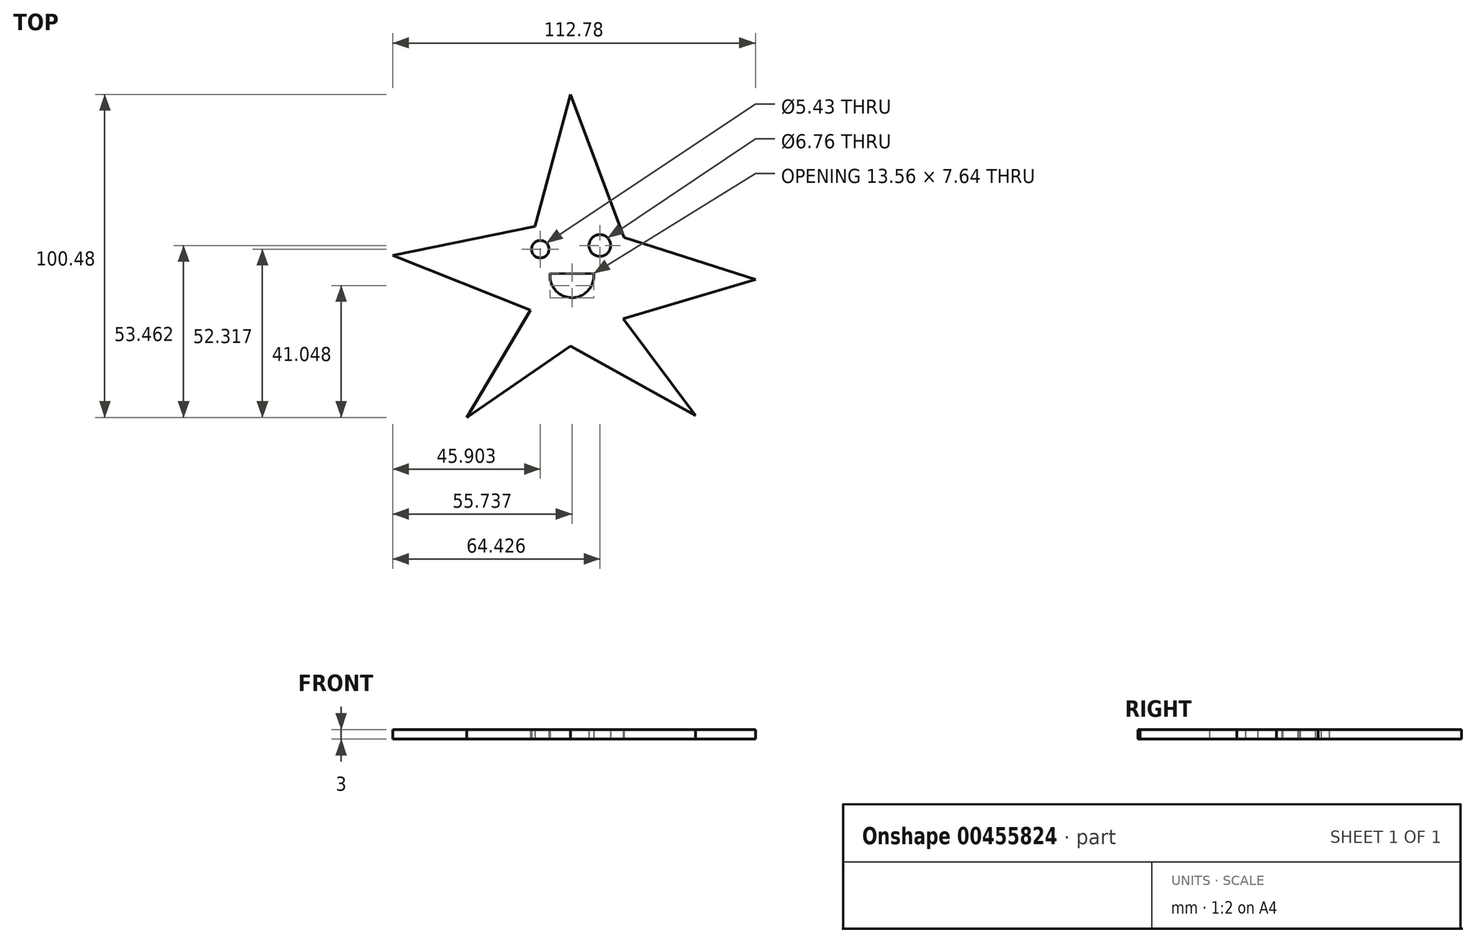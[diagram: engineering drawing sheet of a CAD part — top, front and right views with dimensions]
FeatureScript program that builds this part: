
annotation { "Feature Type Name" : "Feature", "Feature Type Description" : "" }
export const myFeature = defineFeature(function(context is Context, id is Id, definition is map)
    precondition{}
    {
        {
            var Q0;
            Q0=qCreatedBy(makeId("Top.planeOp"),FACE);
            var sketch = newSketch(context, id + "F0", { "sketchPlane" : qUnion([Q0])});
            skLineSegment(sketch, "E0", {"start": v(0, 57.52) * mm, "end": v(16.61, 12.98) * mm});
            skLineSegment(sketch, "E1", {"start": v(16.61, 12.98) * mm, "end": v(57.52, 0) * mm});
            skLineSegment(sketch, "E2", {"start": v(57.52, 0) * mm, "end": v(16.42, -12.22) * mm});
            skLineSegment(sketch, "E3", {"start": v(16.42, -12.22) * mm, "end": v(38.88, -42.38) * mm});
            skLineSegment(sketch, "E4", {"start": v(38.88, -42.38) * mm, "end": v(0, -20.81) * mm});
            skLineSegment(sketch, "E5", {"start": v(0, -20.81) * mm, "end": v(-32.27, -42.96) * mm});
            skLineSegment(sketch, "E6", {"start": v(-32.27, -42.96) * mm, "end": v(-12.41, -9.55) * mm});
            skLineSegment(sketch, "E7", {"start": v(-12.41, -9.55) * mm, "end": v(-55.26, 7.44) * mm});
            skLineSegment(sketch, "E8", {"start": v(-55.26, 7.44) * mm, "end": v(-11.08, 16.42) * mm});
            skLineSegment(sketch, "E9", {"start": v(-11.08, 16.42) * mm, "end": v(0, 57.52) * mm});
            skCircle(sketch, "E10", {"center": v(-9.36, 9.36) * mm, "radius": 2.71 * mm});
            skCircle(sketch, "E11", {"center": v(9.17, 10.5) * mm, "radius": 3.38 * mm});
            skArc(sketch, "E12", {"start": v(-6.3, 1.9) * mm, "mid": v(0.37, -5.73) * mm, "end": v(7.26, 1.72) * mm});
            skLineSegment(sketch, "E13", {"start": v(-6.3, 1.9) * mm, "end": v(7.26, 1.72) * mm});
            skSolve(sketch);
        }
        {
            var Q0;
            Q0=makeQuery(id+"F0.imprint","IMPRINT",FACE,{"disambiguationData":[TD([[makeQuery(id+"F0.imprint","IMPRINT",EDGE,{"derivedFrom":sQuery(id+"F0.wireOp",EDGE,"E0")}),-1.0]])]});
            extrude(context, id + "F1", {"entities" : qUnion([Q0]), "depth" : 3 * mm});
        }
    });
